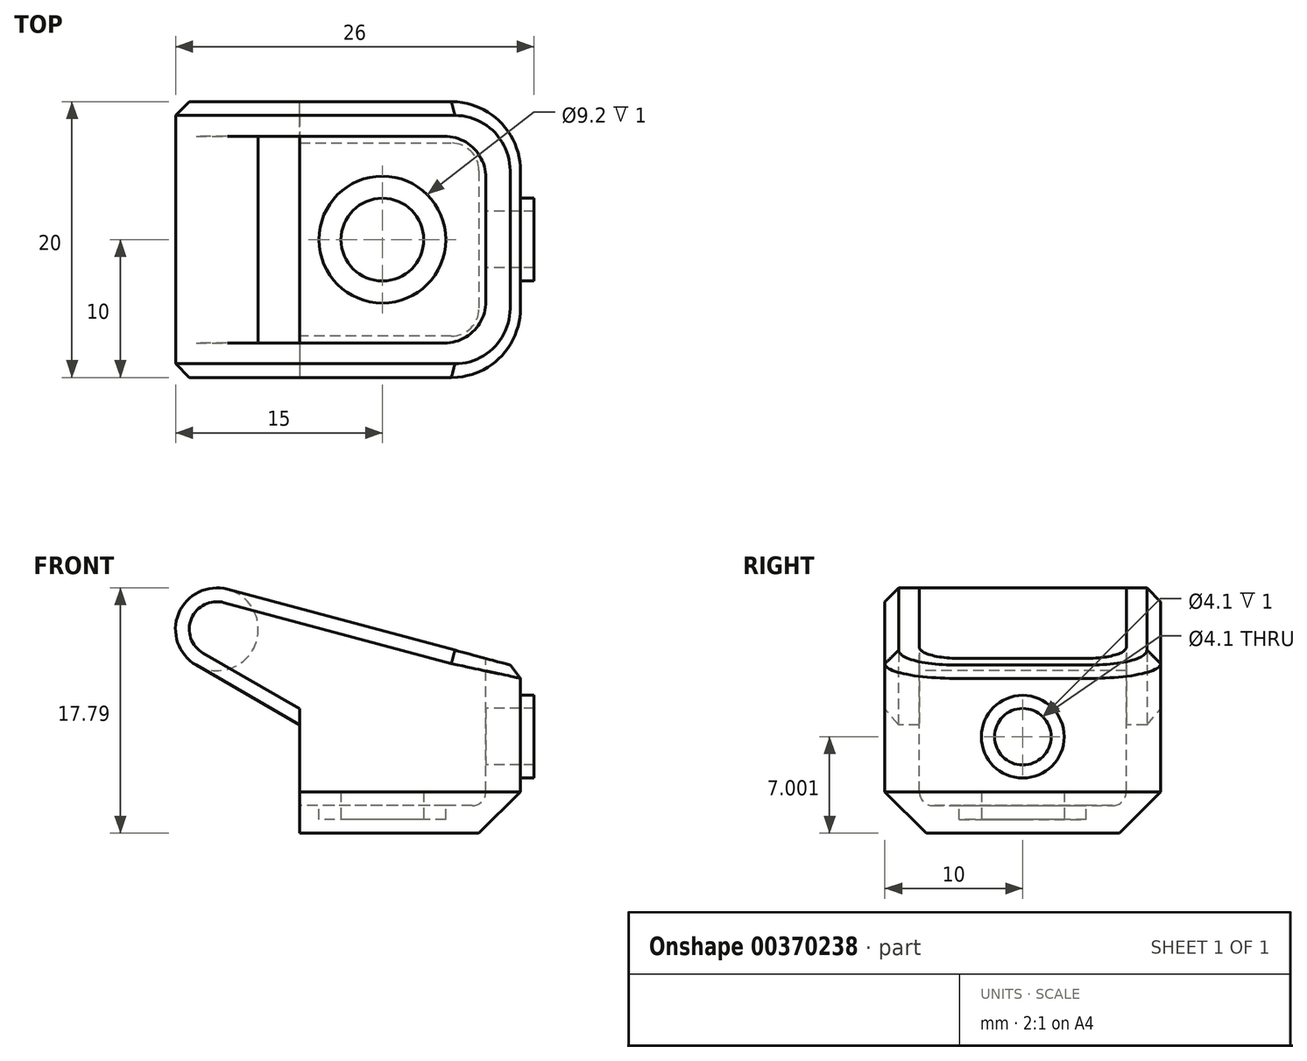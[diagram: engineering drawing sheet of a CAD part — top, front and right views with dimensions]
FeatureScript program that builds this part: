
annotation { "Feature Type Name" : "Feature", "Feature Type Description" : "" }
export const myFeature = defineFeature(function(context is Context, id is Id, definition is map)
    precondition{}
    {
        {
            var Q0;
            Q0=qCreatedBy(makeId("Front.planeOp"),FACE);
            var sketch = newSketch(context, id + "F0", { "sketchPlane" : qUnion([Q0])});
            skLineSegment(sketch, "E0", {"start": v(22, -12.79) * mm, "end": v(22, -0.79) * mm});
            skLineSegment(sketch, "E1", {"start": v(22, -0.79) * mm, "end": v(0.78, 4.9) * mm});
            skLineSegment(sketch, "E2", {"start": v(0, 0) * mm, "end": v(31.98, -8.57) * mm, "construction": true});
            skArc(sketch, "E3", {"start": v(0.78, 4.9) * mm, "mid": v(-2.77, 3.15) * mm, "end": v(-1.5, -0.6) * mm});
            skLineSegment(sketch, "E4", {"start": v(-1.5, -0.6) * mm, "end": v(6, -4.93) * mm});
            skLineSegment(sketch, "E5", {"start": v(-4.1, 2) * mm, "end": v(4.1, 2) * mm, "construction": true});
            skLineSegment(sketch, "E6", {"start": v(0, 7.52) * mm, "end": v(0, 0.49) * mm, "construction": true});
            skLineSegment(sketch, "E7", {"start": v(22, -12.79) * mm, "end": v(6, -12.79) * mm});
            skLineSegment(sketch, "E8", {"start": v(6, -12.79) * mm, "end": v(6, -4.93) * mm});
            skSolve(sketch);
        }
        {
            var Q0;
            Q0=makeQuery(id+"F0.imprint","IMPRINT",FACE,{"disambiguationData":[TD([[makeQuery(id+"F0.imprint","IMPRINT",EDGE,{"derivedFrom":sQuery(id+"F0.wireOp",EDGE,"EPUBpfdk-CZMD-ak17-DREO-DMTnkHclEqKF")}),1.0]])]});
            var Q1;
            Q1=makeQuery(id+"F0.imprint","IMPRINT",FACE,{"disambiguationData":[TD([[makeQuery(id+"F0.imprint","IMPRINT",EDGE,{"derivedFrom":sQuery(id+"F0.wireOp",EDGE,"E0")}),1.0]])]});
            extrude(context, id + "F1", {"entities" : qUnion([Q0, Q1]), "oppositeDirection" : true, "depth" : 20 * mm});
        }
        {
            var Q0;
            Q0=makeQuery(id+"F1.opExtrude","SWEPT_FACE",FACE,{"disambiguationData":[OSD([sQuery(id+"F0.wireOp",EDGE,"E0")])]});
            var sketch = newSketch(context, id + "F2", { "sketchPlane" : qUnion([Q0])});
            skLineSegment(sketch, "E9", {"start": v(0, -5.79) * mm, "end": v(20, -5.79) * mm, "construction": true});
            skLineSegment(sketch, "E10", {"start": v(10, -0.79) * mm, "end": v(10, -12.79) * mm, "construction": true});
            skSolve(sketch);
        }
        {
            var Q0;
            {var subQ0=sQuery(id+"F0.wireOp",EDGE,"E0");Q0=makeQuery(id+"F2.imprint","IMPRINT",FACE,{"disambiguationData":[TD([[makeQuery(id+"F2.imprint","IMPRINT",EDGE,{"derivedFrom":makeQuery(id+"F1.opExtrude","CAP_EDGE",EDGE,{"disambiguationData":[OSD([subQ0])],"isStart":true})}),-1.0]])]});}
            var sketch = newSketch(context, id + "F3", { "sketchPlane" : qUnion([Q0])});
            skCircle(sketch, "E11", {"center": v(10, -5.79) * mm, "radius": 2.05 * mm});
            skSolve(sketch);
        }
        {
            var Q0;
            {var subQ0=sQuery(id+"F0.wireOp",EDGE,"E0");Q0=makeQuery(id+"F2.imprint","IMPRINT",FACE,{"disambiguationData":[TD([[makeQuery(id+"F2.imprint","IMPRINT",EDGE,{"derivedFrom":makeQuery(id+"F1.opExtrude","CAP_EDGE",EDGE,{"disambiguationData":[OSD([subQ0])],"isStart":true})}),-1.0]])]});}
            var sketch = newSketch(context, id + "F4", { "sketchPlane" : qUnion([Q0])});
            skCircle(sketch, "E12", {"center": v(10, -5.79) * mm, "radius": 3 * mm});
            skSolve(sketch);
        }
        {
            var Q0;
            Q0 = qSketchRegion(id + "F4", true);
            extrude(context, id + "F5", {"entities" : qUnion([Q0]), "depth" : 1 * mm});
        }
        {
            var Q0;
            Q0 = qSketchRegion(id + "F3", true);
            extrude(context, id + "F6", {"entities" : qUnion([Q0]), "operationType" : NewBodyOperationType.REMOVE, "endBound" : BoundingType.SYMMETRIC, "depth" : 13.52 * mm});
        }
        {
            var Q0;
            Q0=makeQuery(id+"F1.opExtrude","CAP_FACE",FACE,{"disambiguationData":[OSD([sQuery(id+"F0.wireOp",EDGE,"EPUBpfdk-CZMD-ak17-DREO-DMTnkHclEqKF"),sQuery(id+"F0.wireOp",EDGE,"E0"),sQuery(id+"F0.wireOp",EDGE,"E1"),sQuery(id+"F0.wireOp",EDGE,"IhfXB4BY-18yj-fH0Y-tXZD-5u8uIRlg0mh5")])],"isStart":true});
            var sketch = newSketch(context, id + "F7", { "sketchPlane" : qUnion([Q0])});
            skLineSegment(sketch, "E13", {"start": v(-1.16, -9) * mm, "end": v(-4.42, -7.65) * mm});
            skLineSegment(sketch, "E14", {"start": v(-1.16, -9) * mm, "end": v(-1.16, -10.79) * mm});
            skLineSegment(sketch, "E15", {"start": v(-1.16, -10.79) * mm, "end": v(19.5, -10.79) * mm});
            skLineSegment(sketch, "E16", {"start": v(19.5, 7.14) * mm, "end": v(1.66, 7.03) * mm});
            skArc(sketch, "E17", {"start": v(-1.5, -0.6) * mm, "mid": v(2.77, 0.85) * mm, "end": v(0.78, 4.9) * mm});
            skLineSegment(sketch, "E18", {"start": v(-4.42, -7.65) * mm, "end": v(-1.5, -0.6) * mm});
            skLineSegment(sketch, "E19.trimOffspring", {"start": v(0.78, 4.9) * mm, "end": v(1.66, 7.03) * mm});
            skLineSegment(sketch, "E20", {"start": v(19.5, 7.14) * mm, "end": v(19.5, -10.79) * mm});
            skSolve(sketch);
        }
        {
            var Q0;
            Q0=qCreatedBy(makeId("Top.planeOp"),FACE);
            var sketch = newSketch(context, id + "F8", { "sketchPlane" : qUnion([Q0])});
            skLineSegment(sketch, "E21.bottom", {"start": v(-12.08, 17.5) * mm, "end": v(38.04, 17.5) * mm});
            skLineSegment(sketch, "E21.top", {"start": v(-12.08, 2.5) * mm, "end": v(38.04, 2.5) * mm});
            skLineSegment(sketch, "E21.left", {"start": v(-12.08, 17.5) * mm, "end": v(-12.08, 2.5) * mm});
            skLineSegment(sketch, "E21.right", {"start": v(38.04, 17.5) * mm, "end": v(38.04, 2.5) * mm});
            skSolve(sketch);
        }
        {
            var Q0;
            Q0 = qSketchRegion(id + "F7", true);
            var Q1;
            Q1=makeQuery(id+"F1.opExtrude","CAP_FACE",FACE,{"disambiguationData":[OSD([sQuery(id+"F0.wireOp",EDGE,"EPUBpfdk-CZMD-ak17-DREO-DMTnkHclEqKF"),sQuery(id+"F0.wireOp",EDGE,"E0"),sQuery(id+"F0.wireOp",EDGE,"E1"),sQuery(id+"F0.wireOp",EDGE,"E3"),sQuery(id+"F0.wireOp",EDGE,"E4")])],"isStart":false});
            extrude(context, id + "F9", {"entities" : qUnion([Q0]), "endBound" : BoundingType.UP_TO_SURFACE, "oppositeDirection" : true, "endBoundEntityFace" : qUnion([Q1]), "depth" : 25 * mm});
        }
        {
            var Q0;
            Q0=makeQuery(id+"F8.imprint","IMPRINT",FACE,{"disambiguationData":[TD([[makeQuery(id+"F8.imprint","IMPRINT",EDGE,{"derivedFrom":sQuery(id+"F8.wireOp",EDGE,"E21.bottom")}),-1.0]])]});
            extrude(context, id + "F10", {"entities" : qUnion([Q0]), "depth" : 10.7 * mm, "hasSecondDirection" : true, "secondDirectionOppositeDirection" : true, "secondDirectionDepth" : 12.4 * mm});
        }
        {
            var Q0;
            Q0=makeQuery(id+"F10.opExtrude","SWEPT_BODY",BODY,{"disambiguationData":[OSD([sQuery(id+"F8.wireOp",EDGE,"E21.bottom"),sQuery(id+"F8.wireOp",EDGE,"E21.top"),sQuery(id+"F8.wireOp",EDGE,"E21.left"),sQuery(id+"F8.wireOp",EDGE,"E21.right")])]});
            var Q1;
            Q1=makeQuery(id+"F9.opExtrude","SWEPT_BODY",BODY,{"disambiguationData":[OSD([sQuery(id+"F7.wireOp",EDGE,"E13"),sQuery(id+"F7.wireOp",EDGE,"E14"),sQuery(id+"F7.wireOp",EDGE,"E15"),sQuery(id+"F7.wireOp",EDGE,"E16"),sQuery(id+"F7.wireOp",EDGE,"E17"),sQuery(id+"F7.wireOp",EDGE,"E18"),sQuery(id+"F7.wireOp",EDGE,"E19.trimOffspring"),sQuery(id+"F7.wireOp",EDGE,"E20")])]});
            var Q2;
            Q2=makeQuery(id+"F9.opExtrude","SWEPT_BODY",BODY,{"disambiguationData":[OSD([sQuery(id+"F7.wireOp",EDGE,"E13"),sQuery(id+"F7.wireOp",EDGE,"E14"),sQuery(id+"F7.wireOp",EDGE,"E15"),sQuery(id+"F7.wireOp",EDGE,"E16"),sQuery(id+"F7.wireOp",EDGE,"E17"),sQuery(id+"F7.wireOp",EDGE,"E18"),sQuery(id+"F7.wireOp",EDGE,"E19.trimOffspring"),sQuery(id+"F7.wireOp",EDGE,"E20")])]});
            booleanBodies(context, id + "F11", {"operationType" : BooleanOperationType.INTERSECTION, "tools" : qUnion([Q0, Q1]), "targets" : qUnion([Q2])});
        }
        {
            var Q0;
            Q0=makeQuery(id+"F11.opBoolean","INTERSECT",BODY,{"derivedFrom":[makeQuery(id+"F9.opExtrude","SWEPT_BODY",BODY,{"disambiguationData":[OSD([sQuery(id+"F7.wireOp",EDGE,"E13"),sQuery(id+"F7.wireOp",EDGE,"E14"),sQuery(id+"F7.wireOp",EDGE,"E15"),sQuery(id+"F7.wireOp",EDGE,"E16"),sQuery(id+"F7.wireOp",EDGE,"E17"),sQuery(id+"F7.wireOp",EDGE,"E18"),sQuery(id+"F7.wireOp",EDGE,"E19.trimOffspring"),sQuery(id+"F7.wireOp",EDGE,"E20")])]}),makeQuery(id+"F10.opExtrude","SWEPT_BODY",BODY,{"disambiguationData":[OSD([sQuery(id+"F8.wireOp",EDGE,"E21.bottom"),sQuery(id+"F8.wireOp",EDGE,"E21.top"),sQuery(id+"F8.wireOp",EDGE,"E21.left"),sQuery(id+"F8.wireOp",EDGE,"E21.right")])]})]});
            var Q1;
            Q1=makeQuery(id+"F1.opExtrude","SWEPT_BODY",BODY,{"disambiguationData":[OSD([sQuery(id+"F0.wireOp",EDGE,"EPUBpfdk-CZMD-ak17-DREO-DMTnkHclEqKF"),sQuery(id+"F0.wireOp",EDGE,"E0"),sQuery(id+"F0.wireOp",EDGE,"E1"),sQuery(id+"F0.wireOp",EDGE,"E3"),sQuery(id+"F0.wireOp",EDGE,"E4")])]});
            booleanBodies(context, id + "F12", {"operationType" : BooleanOperationType.SUBTRACTION, "tools" : qUnion([Q0]), "targets" : qUnion([Q1])});
        }
        {
            var Q0;
            Q0=makeQuery(id+"F12.opBoolean","COPY",FACE,{"derivedFrom":makeQuery(id+"F9.opExtrude","SWEPT_FACE",FACE,{"disambiguationData":[OSD([sQuery(id+"F7.wireOp",EDGE,"E15")])]})});
            var sketch = newSketch(context, id + "F13", { "sketchPlane" : qUnion([Q0])});
            skLineSegment(sketch, "E22", {"start": v(6, 10) * mm, "end": v(26.68, 10) * mm, "construction": true});
            skCircle(sketch, "E23", {"center": v(12, 10) * mm, "radius": 4.6 * mm});
            skSolve(sketch);
        }
        {
            var Q0;
            Q0 = qSketchRegion(id + "F13", true);
            extrude(context, id + "F14", {"entities" : qUnion([Q0]), "operationType" : NewBodyOperationType.REMOVE, "oppositeDirection" : true, "depth" : 1 * mm});
        }
        {
            var Q0;
            Q0=makeQuery(id+"F14.boolean.opBoolean","COPY",FACE,{"derivedFrom":makeQuery(id+"F14.opExtrude","CAP_FACE",FACE,{"disambiguationData":[OSD([sQuery(id+"F13.wireOp",EDGE,"E23")])],"isStart":false})});
            var sketch = newSketch(context, id + "F15", { "sketchPlane" : qUnion([Q0])});
            skCircle(sketch, "E24", {"center": v(12, 10) * mm, "radius": 3 * mm});
            skSolve(sketch);
        }
        {
            var Q0;
            Q0 = qSketchRegion(id + "F15", true);
            extrude(context, id + "F16", {"entities" : qUnion([Q0]), "operationType" : NewBodyOperationType.ADD, "depth" : 2 * mm});
        }
        {
            var Q0;
            Q0=makeQuery(id+"F1.opExtrude","CAP_EDGE",EDGE,{"disambiguationData":[OSD([sQuery(id+"F0.wireOp",EDGE,"E0")])],"isStart":true});
            var Q1;
            Q1=makeQuery(id+"F1.opExtrude","CAP_EDGE",EDGE,{"disambiguationData":[OSD([sQuery(id+"F0.wireOp",EDGE,"E0")])],"isStart":false});
            fillet(context, id + "F17", {"entities" : qUnion([Q0, Q1]), "radius" : 5 * mm, "tangentPropagation" : true, "allowEdgeOverflow" : false});
        }
        {
            var Q0;
            Q0=makeQuery(id+"F12.opBoolean","COPY",EDGE,{"derivedFrom":makeQuery(id+"F11.opBoolean","INTERSECT",EDGE,{"derivedFrom":[makeQuery(id+"F9.opExtrude","SWEPT_FACE",FACE,{"disambiguationData":[OSD([sQuery(id+"F7.wireOp",EDGE,"E20")])]}),makeQuery(id+"F10.opExtrude","SWEPT_FACE",FACE,{"disambiguationData":[OSD([sQuery(id+"F8.wireOp",EDGE,"E21.bottom")])]})]})});
            var Q1;
            Q1=makeQuery(id+"F12.opBoolean","COPY",EDGE,{"derivedFrom":makeQuery(id+"F11.opBoolean","INTERSECT",EDGE,{"derivedFrom":[makeQuery(id+"F9.opExtrude","SWEPT_FACE",FACE,{"disambiguationData":[OSD([sQuery(id+"F7.wireOp",EDGE,"E20")])]}),makeQuery(id+"F10.opExtrude","SWEPT_FACE",FACE,{"disambiguationData":[OSD([sQuery(id+"F8.wireOp",EDGE,"E21.top")])]})]})});
            fillet(context, id + "F18", {"entities" : qUnion([Q0, Q1]), "radius" : 3 * mm, "tangentPropagation" : true, "allowEdgeOverflow" : false});
        }
        {
            var Q0;
            Q0=makeQuery(id+"F1.opExtrude","CAP_EDGE",EDGE,{"disambiguationData":[OSD([sQuery(id+"F0.wireOp",EDGE,"E1")])],"isStart":true});
            chamfer(context, id + "F19", {"entities" : qUnion([Q0]), "width" : 1 * mm, "tangentPropagation" : true});
        }
        {
            var Q0;
            Q0=makeQuery(id+"F1.opExtrude","CAP_EDGE",EDGE,{"disambiguationData":[OSD([sQuery(id+"F0.wireOp",EDGE,"E7")])],"isStart":true});
            chamfer(context, id + "F20", {"entities" : qUnion([Q0]), "width" : 3 * mm, "tangentPropagation" : true});
        }
        {
            var Q0;
            Q0=makeQuery(id+"F18.opFillet","BLEND_EDGE",EDGE,{"blendedFrom":[makeQuery(id+"F12.opBoolean","COPY",EDGE,{"derivedFrom":makeQuery(id+"F11.opBoolean","INTERSECT",EDGE,{"derivedFrom":[makeQuery(id+"F9.opExtrude","SWEPT_FACE",FACE,{"disambiguationData":[OSD([sQuery(id+"F7.wireOp",EDGE,"E20")])]}),makeQuery(id+"F10.opExtrude","SWEPT_FACE",FACE,{"disambiguationData":[OSD([sQuery(id+"F8.wireOp",EDGE,"E21.bottom")])]})]})}),makeQuery(id+"F12.opBoolean","COPY",FACE,{"derivedFrom":makeQuery(id+"F9.opExtrude","SWEPT_FACE",FACE,{"disambiguationData":[OSD([sQuery(id+"F7.wireOp",EDGE,"E15")])]})})],"blendedInto":[makeQuery(id+"F12.opBoolean","COPY",FACE,{"derivedFrom":makeQuery(id+"F9.opExtrude","SWEPT_FACE",FACE,{"disambiguationData":[OSD([sQuery(id+"F7.wireOp",EDGE,"E15")])]})})]});
            fillet(context, id + "F21", {"entities" : qUnion([Q0]), "radius" : 1 * mm, "tangentPropagation" : true, "allowEdgeOverflow" : false});
        }
    });
